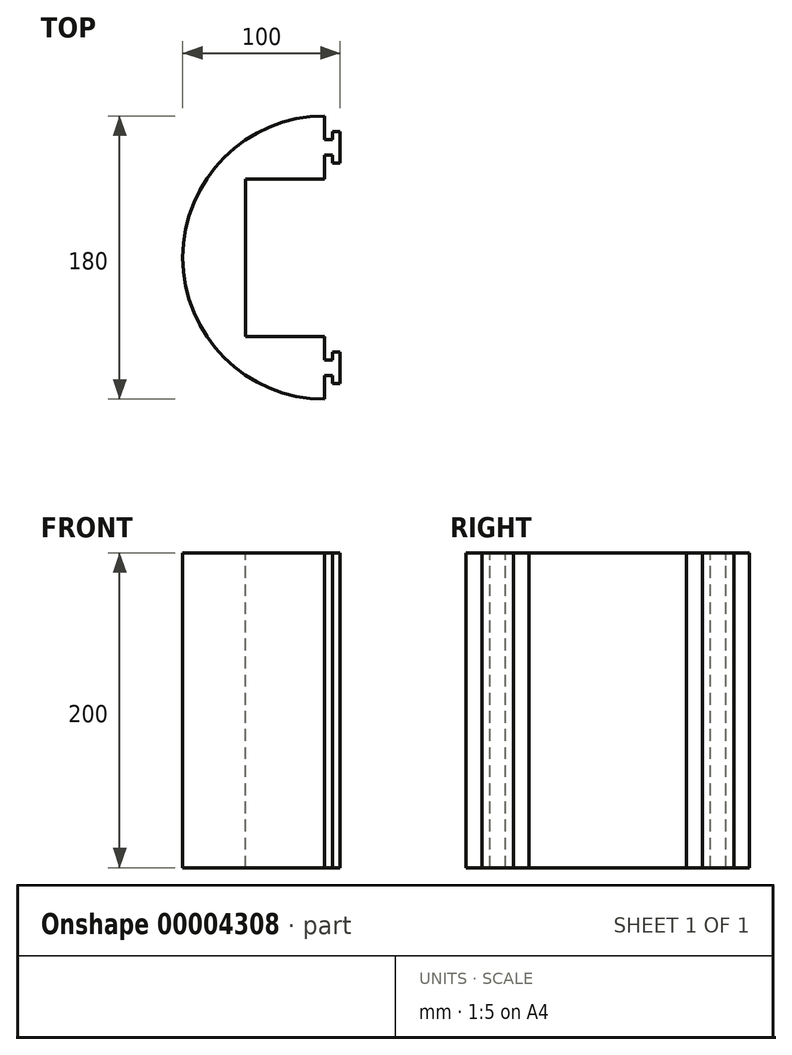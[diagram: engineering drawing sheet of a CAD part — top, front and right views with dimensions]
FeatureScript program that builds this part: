
annotation { "Feature Type Name" : "Feature", "Feature Type Description" : "" }
export const myFeature = defineFeature(function(context is Context, id is Id, definition is map)
    precondition{}
    {
        {
            var Q0;
            Q0=qCreatedBy(makeId("Top.planeOp"),FACE);
            var sketch = newSketch(context, id + "F0", { "sketchPlane" : qUnion([Q0])});
            skArc(sketch, "E0", {"start": v(0, 90) * mm, "mid": v(-90, 0) * mm, "end": v(0, -90) * mm});
            skLineSegment(sketch, "E1", {"start": v(0, -90) * mm, "end": v(0, 90) * mm});
            skLineSegment(sketch, "E2.0", {"start": v(-50, -90) * mm, "end": v(-50, 90) * mm});
            skLineSegment(sketch, "E3", {"start": v(-50, 90) * mm, "end": v(0, 90) * mm});
            skLineSegment(sketch, "E4", {"start": v(-50, -90) * mm, "end": v(0, -90) * mm});
            skLineSegment(sketch, "E5.0", {"start": v(-50, -50) * mm, "end": v(0, -50) * mm});
            skLineSegment(sketch, "E6.0", {"start": v(-50, 50) * mm, "end": v(0, 50) * mm});
            skSolve(sketch);
        }
        {
            var Q0;
            {var subQ0=sQuery(id+"F0.wireOp",EDGE,"E2.0");var subQ1=sQuery(id+"F0.wireOp",EDGE,"E0");var subQ2=makeQuery(id+"F0.imprint","INTERSECT",VERTEX,{"disambiguationData":[OD(0.0)],"derivedFrom":[subQ1,subQ0]});Q0=makeQuery(id+"F0.imprint","IMPRINT",FACE,{"disambiguationData":[TD([[makeQuery(id+"F0.imprint","IMPRINT",EDGE,{"disambiguationData":[TD([[subQ2,-1.0]])],"derivedFrom":subQ1}),1.0]])]});}
            var Q1;
            {var subQ0=sQuery(id+"F0.wireOp",EDGE,"E6.0");Q1=makeQuery(id+"F0.imprint","IMPRINT",FACE,{"disambiguationData":[TD([[makeQuery(id+"F0.imprint","IMPRINT",EDGE,{"derivedFrom":subQ0}),1.0]])]});}
            var Q2;
            {var subQ0=sQuery(id+"F0.wireOp",EDGE,"E5.0");Q2=makeQuery(id+"F0.imprint","IMPRINT",FACE,{"disambiguationData":[TD([[makeQuery(id+"F0.imprint","IMPRINT",EDGE,{"derivedFrom":subQ0}),-1.0]])]});}
            extrude(context, id + "F1", {"entities" : qUnion([Q0, Q1, Q2]), "oppositeDirection" : true, "depth" : 200 * mm});
        }
        {
            var Q0;
            {var subQ0=sQuery(id+"F0.wireOp",EDGE,"E1");Q0=makeQuery(id+"F1.opExtrude","SWEPT_FACE",FACE,{"disambiguationData":[OSD([subQ0]),TDD([makeQuery(id+"F0.imprint","IMPRINT",EDGE,{"disambiguationData":[TD([[makeQuery(id+"F0.imprint","INTERSECT",VERTEX,{"derivedFrom":[subQ0,sQuery(id+"F0.wireOp",EDGE,"E5.0")]}),1.0]])],"derivedFrom":subQ0})])]});}
            var sketch = newSketch(context, id + "F2", { "sketchPlane" : qUnion([Q0])});
            skLineSegment(sketch, "E7.0", {"start": v(-65, -200) * mm, "end": v(-65, 0) * mm});
            skLineSegment(sketch, "E8.0", {"start": v(-75, -200) * mm, "end": v(-75, 0) * mm});
            skLineSegment(sketch, "E9.0", {"start": v(75, -200) * mm, "end": v(75, 0) * mm});
            skLineSegment(sketch, "E10.0", {"start": v(65, -200) * mm, "end": v(65, 0) * mm});
            skLineSegment(sketch, "E11", {"start": v(65, 0) * mm, "end": v(75, 0) * mm});
            skLineSegment(sketch, "E12", {"start": v(65, -200) * mm, "end": v(75, -200) * mm});
            skSolve(sketch);
        }
        {
            var Q0;
            {var subQ4=sQuery(id+"F2.wireOp",EDGE,"E7.0");Q0=makeQuery(id+"F2.imprint","IMPRINT",FACE,{"disambiguationData":[TD([[makeQuery(id+"F2.imprint","IMPRINT",EDGE,{"derivedFrom":subQ4}),1.0]])]});}
            var Q1;
            Q1=makeQuery(id+"F2.imprint","IMPRINT",FACE,{"disambiguationData":[TD([[makeQuery(id+"F2.imprint","IMPRINT",EDGE,{"derivedFrom":sQuery(id+"F2.wireOp",EDGE,"E9.0")}),1.0]])]});
            extrude(context, id + "F3", {"entities" : qUnion([Q0, Q1]), "operationType" : NewBodyOperationType.ADD, "depth" : 10 * mm});
        }
        {
            var Q0;
            Q0=makeQuery(id+"F3.opExtrude","SWEPT_FACE",FACE,{"disambiguationData":[OSD([sQuery(id+"F2.wireOp",EDGE,"E8.0")])]});
            var sketch = newSketch(context, id + "F4", { "sketchPlane" : qUnion([Q0])});
            skLineSegment(sketch, "E13.0", {"start": v(5, -200) * mm, "end": v(5, 0) * mm});
            skSolve(sketch);
        }
        {
            var Q0;
            {var subQ4=sQuery(id+"F4.wireOp",EDGE,"E13.0");Q0=makeQuery(id+"F4.imprint","IMPRINT",FACE,{"disambiguationData":[TD([[makeQuery(id+"F4.imprint","IMPRINT",EDGE,{"derivedFrom":subQ4}),-1.0]])]});}
            extrude(context, id + "F5", {"entities" : qUnion([Q0]), "operationType" : NewBodyOperationType.ADD, "depth" : 5 * mm});
        }
        {
            var Q0;
            Q0=makeQuery(id+"F3.opExtrude","SWEPT_FACE",FACE,{"disambiguationData":[OSD([sQuery(id+"F2.wireOp",EDGE,"E7.0")])]});
            var sketch = newSketch(context, id + "F6", { "sketchPlane" : qUnion([Q0])});
            skLineSegment(sketch, "E14.0", {"start": v(-5, -200) * mm, "end": v(-5, 0) * mm});
            skSolve(sketch);
        }
        {
            var Q0;
            {var subQ4=sQuery(id+"F6.wireOp",EDGE,"E14.0");Q0=makeQuery(id+"F6.imprint","IMPRINT",FACE,{"disambiguationData":[TD([[makeQuery(id+"F6.imprint","IMPRINT",EDGE,{"derivedFrom":subQ4}),1.0]])]});}
            extrude(context, id + "F7", {"entities" : qUnion([Q0]), "operationType" : NewBodyOperationType.ADD, "depth" : 5 * mm});
        }
        {
            var Q0;
            Q0=makeQuery(id+"F3.opExtrude","SWEPT_FACE",FACE,{"disambiguationData":[OSD([sQuery(id+"F2.wireOp",EDGE,"E10.0")])]});
            var sketch = newSketch(context, id + "F8", { "sketchPlane" : qUnion([Q0])});
            skLineSegment(sketch, "E15.0", {"start": v(5, -200) * mm, "end": v(5, 0) * mm});
            skSolve(sketch);
        }
        {
            var Q0;
            {var subQ2=sQuery(id+"F8.wireOp",EDGE,"E15.0");Q0=makeQuery(id+"F8.imprint","IMPRINT",FACE,{"disambiguationData":[TD([[makeQuery(id+"F8.imprint","IMPRINT",EDGE,{"derivedFrom":subQ2}),-1.0]])]});}
            extrude(context, id + "F9", {"entities" : qUnion([Q0]), "operationType" : NewBodyOperationType.ADD, "depth" : 5 * mm});
        }
        {
            var Q0;
            Q0=makeQuery(id+"F3.opExtrude","SWEPT_FACE",FACE,{"disambiguationData":[OSD([sQuery(id+"F2.wireOp",EDGE,"E9.0")])]});
            var sketch = newSketch(context, id + "F10", { "sketchPlane" : qUnion([Q0])});
            skLineSegment(sketch, "E16.0", {"start": v(-5, -200) * mm, "end": v(-5, 0) * mm});
            skSolve(sketch);
        }
        {
            var Q0;
            {var subQ2=sQuery(id+"F10.wireOp",EDGE,"E16.0");Q0=makeQuery(id+"F10.imprint","IMPRINT",FACE,{"disambiguationData":[TD([[makeQuery(id+"F10.imprint","IMPRINT",EDGE,{"derivedFrom":subQ2}),1.0]])]});}
            extrude(context, id + "F11", {"entities" : qUnion([Q0]), "operationType" : NewBodyOperationType.ADD, "depth" : 5 * mm});
        }
    });
